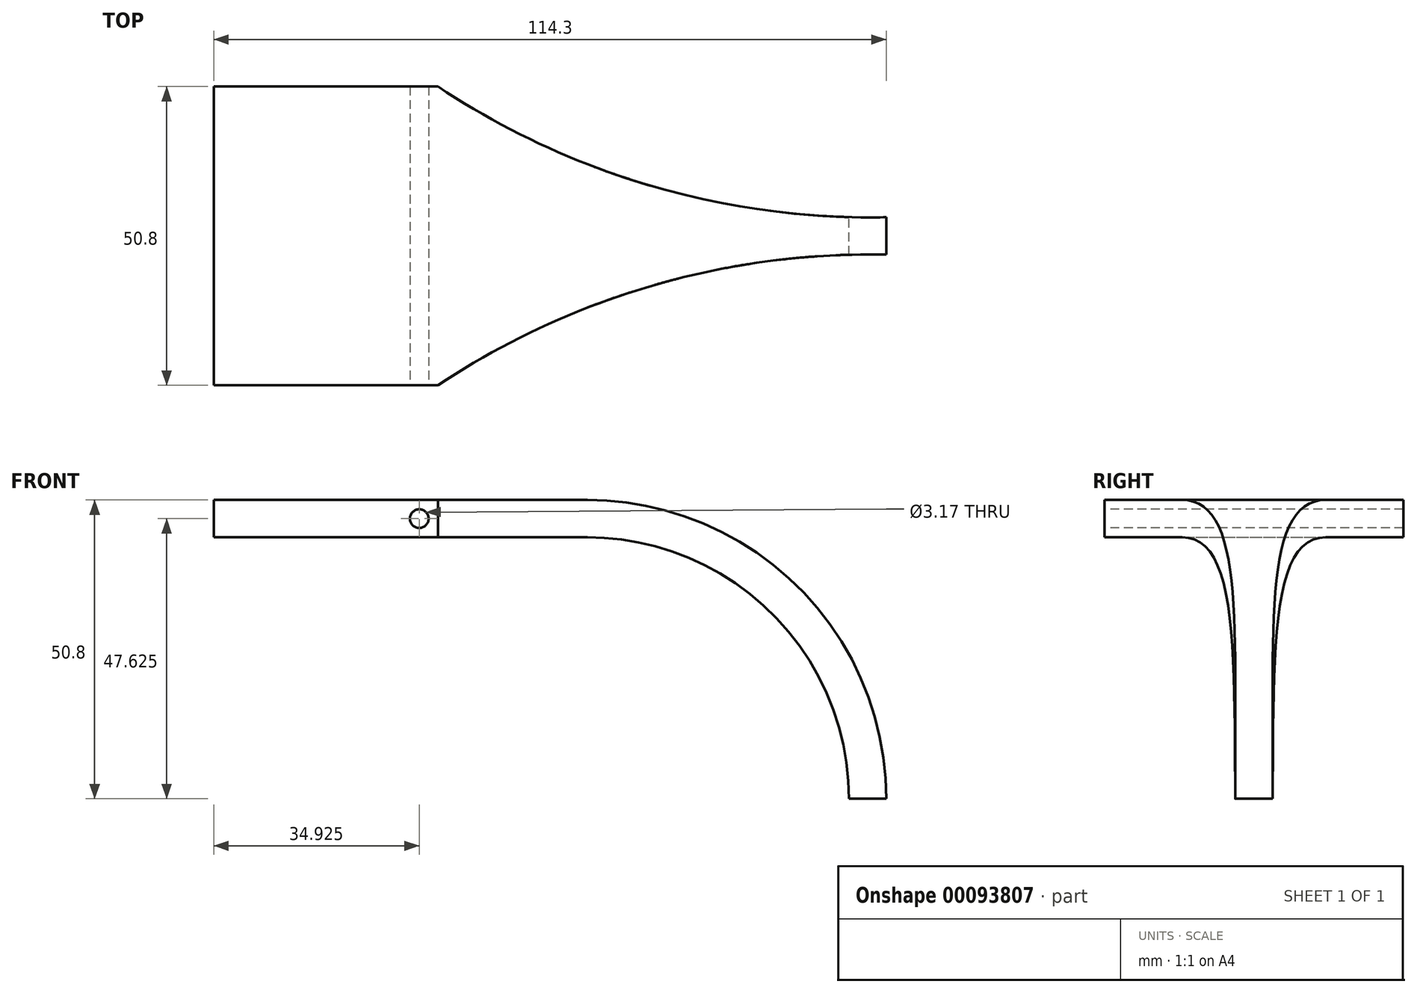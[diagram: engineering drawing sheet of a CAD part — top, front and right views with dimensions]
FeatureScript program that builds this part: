
annotation { "Feature Type Name" : "Feature", "Feature Type Description" : "" }
export const myFeature = defineFeature(function(context is Context, id is Id, definition is map)
    precondition{}
    {
        {
            var Q0;
            Q0=qCreatedBy(makeId("Front.planeOp"),FACE);
            var sketch = newSketch(context, id + "F0", { "sketchPlane" : qUnion([Q0])});
            skLineSegment(sketch, "E0", {"start": v(0, 0) * mm, "end": v(0, 6.35) * mm});
            skLineSegment(sketch, "E1", {"start": v(0, 6.35) * mm, "end": v(25.4, 6.35) * mm});
            skLineSegment(sketch, "E2", {"start": v(0, 0) * mm, "end": v(25.4, 0) * mm});
            skArc(sketch, "E3", {"start": v(76.2, -44.45) * mm, "mid": v(61.32, -8.53) * mm, "end": v(25.4, 6.35) * mm});
            skArc(sketch, "E4", {"start": v(69.85, -44.45) * mm, "mid": v(56.83, -13.02) * mm, "end": v(25.4, 0) * mm});
            skLineSegment(sketch, "E5", {"start": v(69.85, -44.45) * mm, "end": v(76.2, -44.45) * mm});
            skSolve(sketch);
        }
        {
            var Q0;
            Q0 = qSketchRegion(id + "F0", true);
            extrude(context, id + "F1", {"entities" : qUnion([Q0]), "depth" : 50.8 * mm});
        }
        {
            var Q0;
            Q0=makeQuery(id+"F1.opExtrude","SWEPT_FACE",FACE,{"disambiguationData":[OSD([sQuery(id+"F0.wireOp",EDGE,"E1")])]});
            var sketch = newSketch(context, id + "F2", { "sketchPlane" : qUnion([Q0])});
            skLineSegment(sketch, "E6", {"start": v(0, -50.8) * mm, "end": v(76.2, -50.8) * mm});
            skPoint(sketch, "E6.endSnap0", {"position": v(12.7, -50.8) * mm});
            skLineSegment(sketch, "E7", {"start": v(76.2, -50.8) * mm, "end": v(76.2, -28.58) * mm});
            skLineSegment(sketch, "E8", {"start": v(0, 0) * mm, "end": v(76.2, 0) * mm});
            skLineSegment(sketch, "E9", {"start": v(76.2, 0) * mm, "end": v(76.2, -22.23) * mm});
            skArc(sketch, "E10", {"start": v(76.2, -28.57) * mm, "mid": v(36.4, -33.86) * mm, "end": v(0, -50.8) * mm});
            skArc(sketch, "E11", {"start": v(0, 0) * mm, "mid": v(36.4, -16.94) * mm, "end": v(76.2, -22.23) * mm});
            skSolve(sketch);
        }
        {
            var Q0;
            Q0 = qSketchRegion(id + "F2", true);
            extrude(context, id + "F3", {"entities" : qUnion([Q0]), "operationType" : NewBodyOperationType.REMOVE, "endBound" : BoundingType.THROUGH_ALL, "oppositeDirection" : true, "depth" : 25.4 * mm});
        }
        {
            var Q0;
            Q0=makeQuery(id+"F1.opExtrude","SWEPT_FACE",FACE,{"disambiguationData":[OSD([sQuery(id+"F0.wireOp",EDGE,"E0")])]});
            var sketch = newSketch(context, id + "F4", { "sketchPlane" : qUnion([Q0])});
            skLineSegment(sketch, "E12.bottom", {"start": v(0, 0) * mm, "end": v(50.8, 0) * mm});
            skLineSegment(sketch, "E12.top", {"start": v(0, 6.35) * mm, "end": v(50.8, 6.35) * mm});
            skLineSegment(sketch, "E12.left", {"start": v(0, 0) * mm, "end": v(0, 6.35) * mm});
            skLineSegment(sketch, "E12.right", {"start": v(50.8, 0) * mm, "end": v(50.8, 6.35) * mm});
            skSolve(sketch);
        }
        {
            var Q0;
            Q0 = qSketchRegion(id + "F4", true);
            extrude(context, id + "F5", {"entities" : qUnion([Q0]), "operationType" : NewBodyOperationType.ADD, "depth" : 38.1 * mm});
        }
        {
            var Q0;
            Q0=makeQuery(id+"F5.opExtrude","SWEPT_FACE",FACE,{"disambiguationData":[OSD([sQuery(id+"F4.wireOp",EDGE,"E12.right")])]});
            var sketch = newSketch(context, id + "F6", { "sketchPlane" : qUnion([Q0])});
            skCircle(sketch, "E13", {"center": v(-3.18, 3.18) * mm, "radius": 1.59 * mm});
            skSolve(sketch);
        }
        {
            var Q0;
            Q0 = qSketchRegion(id + "F6", true);
            extrude(context, id + "F7", {"entities" : qUnion([Q0]), "operationType" : NewBodyOperationType.REMOVE, "endBound" : BoundingType.THROUGH_ALL, "oppositeDirection" : true, "depth" : 25.4 * mm});
        }
    });
